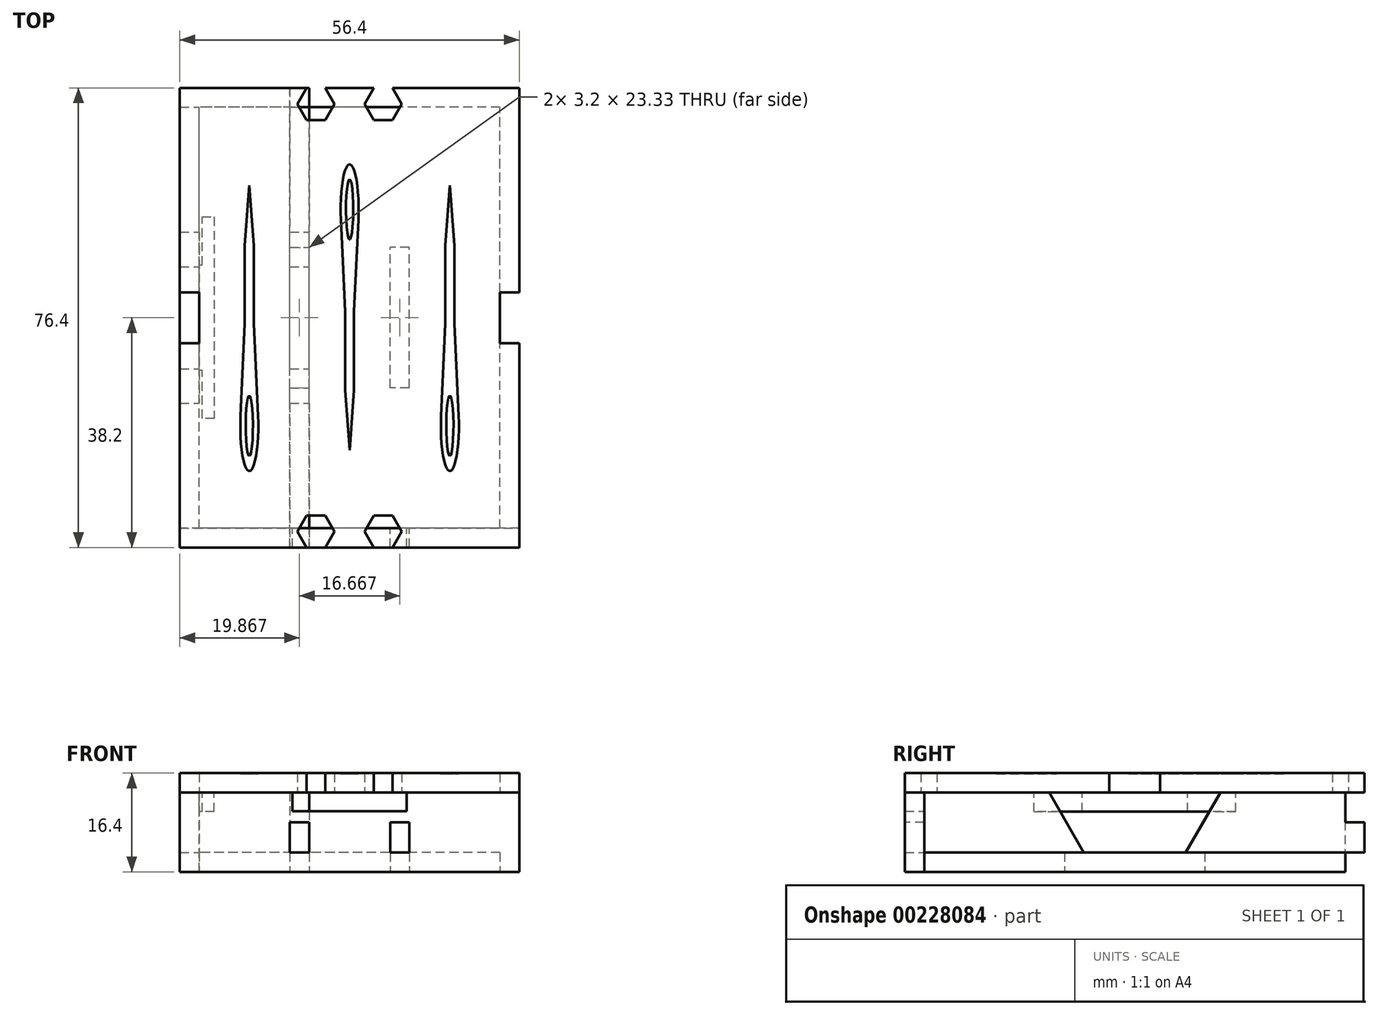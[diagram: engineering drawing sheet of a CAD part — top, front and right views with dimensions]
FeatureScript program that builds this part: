
annotation { "Feature Type Name" : "Feature", "Feature Type Description" : "" }
export const myFeature = defineFeature(function(context is Context, id is Id, definition is map)
    precondition{}
    {
        {
            assignVariable(context, id + "F0", {"name" : "mat_thickness", "anyValue" : 3.2 * mm});
        }
        {
            var Q0;
            Q0=qCreatedBy(makeId("Top.planeOp"),FACE);
            var sketch = newSketch(context, id + "F1", { "sketchPlane" : qUnion([Q0])});
            skLineSegment(sketch, "E0.bottom", {"start": v(25, -35) * mm, "end": v(-25, -35) * mm});
            skLineSegment(sketch, "E0.top", {"start": v(25, 35) * mm, "end": v(-25, 35) * mm});
            skLineSegment(sketch, "E0.left", {"start": v(25, -35) * mm, "end": v(25, 35) * mm});
            skLineSegment(sketch, "E0.right", {"start": v(-25, -35) * mm, "end": v(-25, 35) * mm});
            skPoint(sketch, "E0.middle", {"position": v(0, 0) * mm});
            skLineSegment(sketch, "E1.bottom", {"start": v(-6.73, -11.67) * mm, "end": v(-9.93, -11.67) * mm});
            skLineSegment(sketch, "E1.top", {"start": v(-6.73, 11.67) * mm, "end": v(-9.93, 11.67) * mm});
            skLineSegment(sketch, "E1.left", {"start": v(-6.73, -11.67) * mm, "end": v(-6.73, 11.67) * mm});
            skLineSegment(sketch, "E1.right", {"start": v(-9.93, -11.67) * mm, "end": v(-9.93, 11.67) * mm});
            skPoint(sketch, "E1.middle", {"position": v(-8.33, 0) * mm});
            skPoint(sketch, "E2.1.0.0", {"position": v(8.33, 0) * mm});
            skLineSegment(sketch, "E2.1.0.1", {"start": v(9.93, -11.67) * mm, "end": v(9.93, 11.67) * mm});
            skLineSegment(sketch, "E2.1.0.2", {"start": v(6.73, -11.67) * mm, "end": v(6.73, 11.67) * mm});
            skLineSegment(sketch, "E2.1.0.3", {"start": v(9.93, -11.67) * mm, "end": v(6.73, -11.67) * mm});
            skLineSegment(sketch, "E2.1.0.4", {"start": v(9.93, 11.67) * mm, "end": v(6.73, 11.67) * mm});
            skLineSegment(sketch, "E2.direction1", {"start": v(-9.93, -11.67) * mm, "end": v(6.73, -11.67) * mm, "construction": true});
            skSolve(sketch);
        }
        {
            var Q0;
            Q0=makeQuery(id+"F1.imprint","IMPRINT",FACE,{"disambiguationData":[TD([[makeQuery(id+"F1.imprint","IMPRINT",EDGE,{"derivedFrom":sQuery(id+"F1.wireOp",EDGE,"E0.bottom")}),-1.0]])]});
            extrude(context, id + "F2", {"entities" : qUnion([Q0]), "depth" : getVariable(context, 'mat_thickness')});
        }
        {
            var Q0;
            Q0=makeQuery(id+"F2.opExtrude","SWEPT_FACE",FACE,{"disambiguationData":[OSD([sQuery(id+"F1.wireOp",EDGE,"E0.right")])]});
            var sketch = newSketch(context, id + "F3", { "sketchPlane" : qUnion([Q0])});
            skLineSegment(sketch, "E3", {"start": v(-35, 0) * mm, "end": v(-35, 13.2) * mm});
            skLineSegment(sketch, "E4.0", {"start": v(35, 0) * mm, "end": v(-35, 0) * mm});
            skLineSegment(sketch, "E5", {"start": v(35, 0) * mm, "end": v(35, 13.2) * mm});
            skLineSegment(sketch, "E6", {"start": v(35, 13.2) * mm, "end": v(14.24, 13.2) * mm});
            skLineSegment(sketch, "E7", {"start": v(14.24, 13.2) * mm, "end": v(8.47, 3.2) * mm});
            skLineSegment(sketch, "E8", {"start": v(8.47, 3.2) * mm, "end": v(-8.47, 3.2) * mm});
            skLineSegment(sketch, "E9", {"start": v(-8.47, 3.2) * mm, "end": v(-14.24, 13.2) * mm});
            skLineSegment(sketch, "E10", {"start": v(-14.24, 13.2) * mm, "end": v(-35, 13.2) * mm});
            skLineSegment(sketch, "E11", {"start": v(0, -7.06) * mm, "end": v(0, 22.7) * mm, "construction": true});
            skSolve(sketch);
        }
        {
            var Q0;
            Q0 = qSketchRegion(id + "F3", true);
            extrude(context, id + "F4", {"entities" : qUnion([Q0]), "depth" : getVariable(context, 'mat_thickness')});
        }
        {
            var Q0;
            Q0=makeQuery(id+"F2.opExtrude","SWEPT_FACE",FACE,{"disambiguationData":[OSD([sQuery(id+"F1.wireOp",EDGE,"E1.left")])]});
            var sketch = newSketch(context, id + "F5", { "sketchPlane" : qUnion([Q0])});
            skLineSegment(sketch, "E12", {"start": v(38.2, 8.2) * mm, "end": v(38.2, 3.2) * mm});
            skLineSegment(sketch, "E13", {"start": v(38.2, 3.2) * mm, "end": v(35, 3.2) * mm});
            skLineSegment(sketch, "E14", {"start": v(35, 3.2) * mm, "end": v(35, 3.2) * mm});
            skLineSegment(sketch, "E15", {"start": v(35, 3.2) * mm, "end": v(11.67, 3.2) * mm});
            skLineSegment(sketch, "E16", {"start": v(11.67, 3.2) * mm, "end": v(11.67, 0) * mm});
            skLineSegment(sketch, "E17", {"start": v(11.67, 0) * mm, "end": v(-11.67, 0) * mm});
            skLineSegment(sketch, "E18", {"start": v(-11.67, 0) * mm, "end": v(-11.67, 3.2) * mm});
            skLineSegment(sketch, "E19", {"start": v(-11.67, 3.2) * mm, "end": v(-35, 3.2) * mm});
            skLineSegment(sketch, "E20", {"start": v(-35, 3.2) * mm, "end": v(-35, 3.2) * mm});
            skLineSegment(sketch, "E21", {"start": v(-35, 3.2) * mm, "end": v(-38.2, 3.2) * mm});
            skLineSegment(sketch, "E22", {"start": v(-38.2, 3.2) * mm, "end": v(-38.2, 8.2) * mm});
            skLineSegment(sketch, "E23", {"start": v(-38.2, 8.2) * mm, "end": v(-35, 8.2) * mm});
            skLineSegment(sketch, "E24", {"start": v(-35, 8.2) * mm, "end": v(-35, 13.2) * mm});
            skLineSegment(sketch, "E25", {"start": v(-35, 13.2) * mm, "end": v(35, 13.2) * mm});
            skLineSegment(sketch, "E26", {"start": v(35, 13.2) * mm, "end": v(35, 8.2) * mm});
            skLineSegment(sketch, "E27", {"start": v(35, 8.2) * mm, "end": v(38.2, 8.2) * mm});
            skLineSegment(sketch, "E28", {"start": v(0, -9.88) * mm, "end": v(0, 20.89) * mm, "construction": true});
            skPoint(sketch, "E28.startSnap0", {"position": v(0, 0) * mm});
            skLineSegment(sketch, "E29", {"start": v(14.24, 13.2) * mm, "end": v(8.47, 3.2) * mm});
            skLineSegment(sketch, "E30", {"start": v(8.47, 3.2) * mm, "end": v(-8.47, 3.2) * mm});
            skLineSegment(sketch, "E31", {"start": v(-8.47, 3.2) * mm, "end": v(-14.24, 13.2) * mm});
            skSolve(sketch);
        }
        {
            var Q0;
            Q0=makeQuery(id+"F5.imprint","IMPRINT",FACE,{"disambiguationData":[TD([[makeQuery(id+"F5.imprint","IMPRINT",EDGE,{"derivedFrom":sQuery(id+"F5.wireOp",EDGE,"E12")}),-1.0]])]});
            var Q1;
            {var subQ0=sQuery(id+"F5.wireOp",EDGE,"E19");Q1=makeQuery(id+"F5.imprint","IMPRINT",FACE,{"disambiguationData":[TD([[makeQuery(id+"F5.imprint","IMPRINT",EDGE,{"derivedFrom":subQ0}),-1.0]])]});}
            var Q2;
            {var subQ1=sQuery(id+"F5.wireOp",EDGE,"E16");Q2=makeQuery(id+"F5.imprint","IMPRINT",FACE,{"disambiguationData":[TD([[makeQuery(id+"F5.imprint","IMPRINT",EDGE,{"derivedFrom":subQ1}),-1.0]])]});}
            extrude(context, id + "F6", {"entities" : qUnion([Q0, Q1, Q2]), "depth" : getVariable(context, 'mat_thickness')});
        }
        {
            var Q0;
            Q0=makeQuery(id+"F2.opExtrude","SWEPT_FACE",FACE,{"disambiguationData":[OSD([sQuery(id+"F1.wireOp",EDGE,"E0.bottom")])]});
            var sketch = newSketch(context, id + "F7", { "sketchPlane" : qUnion([Q0])});
            skLineSegment(sketch, "E32.0", {"start": v(-28.2, 0) * mm, "end": v(-25, 0) * mm});
            skLineSegment(sketch, "E32.1", {"start": v(25, 0) * mm, "end": v(-25, 0) * mm});
            skLineSegment(sketch, "E32.2", {"start": v(-28.2, 0) * mm, "end": v(-28.2, 13.2) * mm});
            skLineSegment(sketch, "E33", {"start": v(-28.2, 13.2) * mm, "end": v(25, 13.2) * mm});
            skLineSegment(sketch, "E34", {"start": v(25, 13.2) * mm, "end": v(25, 0) * mm});
            skLineSegment(sketch, "E35.bottom", {"start": v(-6.73, 8.2) * mm, "end": v(-9.93, 8.2) * mm});
            skLineSegment(sketch, "E35.top", {"start": v(-6.73, 3.2) * mm, "end": v(-9.93, 3.2) * mm});
            skLineSegment(sketch, "E35.left", {"start": v(-6.73, 8.2) * mm, "end": v(-6.73, 3.2) * mm});
            skLineSegment(sketch, "E35.right", {"start": v(-9.93, 8.2) * mm, "end": v(-9.93, 3.2) * mm});
            skPoint(sketch, "E35.middle", {"position": v(-8.33, 5.7) * mm});
            skLineSegment(sketch, "E36", {"start": v(-25, 3.2) * mm, "end": v(-25, 13.2) * mm, "construction": true});
            skPoint(sketch, "E37.startSnap0", {"position": v(-25, 8.2) * mm});
            skLineSegment(sketch, "E38.1.0.0", {"start": v(9.93, 8.2) * mm, "end": v(9.93, 3.2) * mm});
            skLineSegment(sketch, "E38.1.0.1", {"start": v(6.73, 8.2) * mm, "end": v(6.73, 3.2) * mm});
            skLineSegment(sketch, "E38.1.0.2", {"start": v(9.93, 3.2) * mm, "end": v(6.73, 3.2) * mm});
            skPoint(sketch, "E38.1.0.3", {"position": v(8.33, 5.7) * mm});
            skLineSegment(sketch, "E38.1.0.4", {"start": v(9.93, 8.2) * mm, "end": v(6.73, 8.2) * mm});
            skLineSegment(sketch, "E38.direction1", {"start": v(-9.93, 3.2) * mm, "end": v(6.73, 3.2) * mm, "construction": true});
            skLineSegment(sketch, "E39", {"start": v(25, 13.2) * mm, "end": v(28.2, 13.2) * mm});
            skLineSegment(sketch, "E40", {"start": v(28.2, 13.2) * mm, "end": v(28.2, 0) * mm});
            skLineSegment(sketch, "E41", {"start": v(28.2, 0) * mm, "end": v(25, 0) * mm});
            skLineSegment(sketch, "E42", {"start": v(9.5, 13.2) * mm, "end": v(9.5, 10.1) * mm});
            skLineSegment(sketch, "E43", {"start": v(9.5, 10.1) * mm, "end": v(-9.5, 10.1) * mm});
            skLineSegment(sketch, "E44", {"start": v(-9.5, 10.1) * mm, "end": v(-9.5, 13.2) * mm});
            skLineSegment(sketch, "E45", {"start": v(0, -5.67) * mm, "end": v(0, 16.81) * mm, "construction": true});
            skSolve(sketch);
        }
        {
            var Q0;
            {var subQ0=sQuery(id+"F7.wireOp",EDGE,"E39");Q0=makeQuery(id+"F7.imprint","IMPRINT",FACE,{"disambiguationData":[TD([[makeQuery(id+"F7.imprint","IMPRINT",EDGE,{"derivedFrom":subQ0}),-1.0]])]});}
            var Q1;
            {var subQ2=sQuery(id+"F7.wireOp",EDGE,"E32.1");Q1=makeQuery(id+"F7.imprint","IMPRINT",FACE,{"disambiguationData":[TD([[makeQuery(id+"F7.imprint","IMPRINT",EDGE,{"derivedFrom":subQ2}),-1.0]])]});}
            var Q2;
            Q2=makeQuery(id+"F7.imprint","IMPRINT",FACE,{"disambiguationData":[TD([[makeQuery(id+"F7.imprint","IMPRINT",EDGE,{"derivedFrom":sQuery(id+"F7.wireOp",EDGE,"E32.0")}),1.0]])]});
            extrude(context, id + "F8", {"entities" : qUnion([Q0, Q1, Q2]), "depth" : getVariable(context, 'mat_thickness')});
        }
        {
            var Q0;
            Q0=makeQuery(id+"F4.opExtrude","CAP_FACE",FACE,{"disambiguationData":[OSD([sQuery(id+"F3.wireOp",EDGE,"E3"),sQuery(id+"F3.wireOp",EDGE,"E4.0"),sQuery(id+"F3.wireOp",EDGE,"E5"),sQuery(id+"F3.wireOp",EDGE,"E6"),sQuery(id+"F3.wireOp",EDGE,"E7"),sQuery(id+"F3.wireOp",EDGE,"E8"),sQuery(id+"F3.wireOp",EDGE,"E9"),sQuery(id+"F3.wireOp",EDGE,"E10")])],"isStart":false});
            var sketch = newSketch(context, id + "F9", { "sketchPlane" : qUnion([Q0])});
            skLineSegment(sketch, "E46.0", {"start": v(-8.47, 3.2) * mm, "end": v(-14.24, 13.2) * mm});
            skLineSegment(sketch, "E46.1", {"start": v(8.47, 3.2) * mm, "end": v(-8.47, 3.2) * mm});
            skLineSegment(sketch, "E46.2", {"start": v(14.24, 13.2) * mm, "end": v(8.47, 3.2) * mm});
            skLineSegment(sketch, "E47", {"start": v(-14.24, 13.2) * mm, "end": v(-4.23, 13.2) * mm});
            skLineSegment(sketch, "E48", {"start": v(-4.23, 13.2) * mm, "end": v(-4.23, 16.4) * mm});
            skLineSegment(sketch, "E49", {"start": v(-4.23, 16.4) * mm, "end": v(4.23, 16.4) * mm});
            skLineSegment(sketch, "E50", {"start": v(4.23, 16.4) * mm, "end": v(4.23, 13.2) * mm});
            skLineSegment(sketch, "E51", {"start": v(4.23, 13.2) * mm, "end": v(14.24, 13.2) * mm});
            skLineSegment(sketch, "E52", {"start": v(0, -3.65) * mm, "end": v(0, 23.25) * mm, "construction": true});
            skSolve(sketch);
        }
        {
            var Q0;
            Q0 = qSketchRegion(id + "F9", true);
            extrude(context, id + "F10", {"entities" : qUnion([Q0]), "oppositeDirection" : true, "depth" : getVariable(context, 'mat_thickness')});
        }
        {
            var Q0;
            Q0=makeQuery(id+"F8.opExtrude","SWEPT_FACE",FACE,{"disambiguationData":[OSD([sQuery(id+"F7.wireOp",EDGE,"E33"),sQuery(id+"F7.wireOp",EDGE,"E39")])]});
            var sketch = newSketch(context, id + "F11", { "sketchPlane" : qUnion([Q0])});
            skLineSegment(sketch, "E53.1", {"start": v(-28.2, 4.23) * mm, "end": v(-28.2, -4.23) * mm});
            skLineSegment(sketch, "E54", {"start": v(-28.2, -38.2) * mm, "end": v(-28.2, 38.2) * mm});
            skLineSegment(sketch, "E55", {"start": v(-28.2, 38.2) * mm, "end": v(28.2, 38.2) * mm});
            skLineSegment(sketch, "E56", {"start": v(28.2, 38.2) * mm, "end": v(28.2, -38.2) * mm});
            skLineSegment(sketch, "E57", {"start": v(-28.2, 4.23) * mm, "end": v(-25, 4.23) * mm});
            skLineSegment(sketch, "E58", {"start": v(-25, 4.23) * mm, "end": v(-25, -4.23) * mm});
            skLineSegment(sketch, "E59", {"start": v(-25, -4.23) * mm, "end": v(-28.2, -4.23) * mm});
            skLineSegment(sketch, "E60", {"start": v(28.2, 4.23) * mm, "end": v(25, 4.23) * mm});
            skLineSegment(sketch, "E61", {"start": v(25, 4.23) * mm, "end": v(25, -4.23) * mm});
            skPoint(sketch, "E61.endSnap0", {"position": v(-26.6, -4.23) * mm});
            skLineSegment(sketch, "E62", {"start": v(25, -4.23) * mm, "end": v(28.2, -4.23) * mm});
            skLineSegment(sketch, "E63", {"start": v(-28.2, -38.2) * mm, "end": v(28.2, -38.2) * mm});
            skPoint(sketch, "E64.0", {"position": v(-28.2, -38.2) * mm});
            skCircle(sketch, "E65.cCircle", {"center": v(5.59, -35.53) * mm, "radius": 3.09 * mm, "construction": true});
            skLineSegment(sketch, "E65.0", {"start": v(7.13, -38.2) * mm, "end": v(4.04, -38.2) * mm});
            skLineSegment(sketch, "E65.1", {"start": v(4.04, -38.2) * mm, "end": v(2.5, -35.53) * mm});
            skLineSegment(sketch, "E65.2", {"start": v(2.5, -35.53) * mm, "end": v(4.04, -32.85) * mm});
            skLineSegment(sketch, "E65.3", {"start": v(4.04, -32.85) * mm, "end": v(7.13, -32.85) * mm});
            skLineSegment(sketch, "E65.4", {"start": v(7.13, -32.85) * mm, "end": v(8.68, -35.53) * mm});
            skLineSegment(sketch, "E65.5", {"start": v(8.68, -35.53) * mm, "end": v(7.13, -38.2) * mm});
            skCircle(sketch, "E66.cCircle", {"center": v(-5.59, -35.53) * mm, "radius": 3.09 * mm, "construction": true});
            skLineSegment(sketch, "E66.0", {"start": v(-4.04, -38.2) * mm, "end": v(-7.13, -38.2) * mm});
            skLineSegment(sketch, "E66.1", {"start": v(-7.13, -38.2) * mm, "end": v(-8.68, -35.53) * mm});
            skLineSegment(sketch, "E66.2", {"start": v(-8.68, -35.53) * mm, "end": v(-7.13, -32.85) * mm});
            skLineSegment(sketch, "E66.3", {"start": v(-7.13, -32.85) * mm, "end": v(-4.04, -32.85) * mm});
            skLineSegment(sketch, "E66.4", {"start": v(-4.04, -32.85) * mm, "end": v(-2.5, -35.53) * mm});
            skLineSegment(sketch, "E66.5", {"start": v(-2.5, -35.53) * mm, "end": v(-4.04, -38.2) * mm});
            skCircle(sketch, "E67.cCircle", {"center": v(5.59, 35.52) * mm, "radius": 3.09 * mm, "construction": true});
            skLineSegment(sketch, "E67.0", {"start": v(7.13, 32.85) * mm, "end": v(4.04, 32.85) * mm});
            skLineSegment(sketch, "E67.1", {"start": v(4.04, 32.85) * mm, "end": v(2.5, 35.52) * mm});
            skLineSegment(sketch, "E67.2", {"start": v(2.5, 35.52) * mm, "end": v(4.04, 38.2) * mm});
            skLineSegment(sketch, "E67.3", {"start": v(4.04, 38.2) * mm, "end": v(7.13, 38.2) * mm});
            skLineSegment(sketch, "E67.4", {"start": v(7.13, 38.2) * mm, "end": v(8.68, 35.52) * mm});
            skLineSegment(sketch, "E67.5", {"start": v(8.68, 35.52) * mm, "end": v(7.13, 32.85) * mm});
            skCircle(sketch, "E68.cCircle", {"center": v(-5.59, 35.52) * mm, "radius": 3.09 * mm, "construction": true});
            skLineSegment(sketch, "E68.0", {"start": v(-4.04, 32.85) * mm, "end": v(-7.13, 32.85) * mm});
            skLineSegment(sketch, "E68.1", {"start": v(-7.13, 32.85) * mm, "end": v(-8.68, 35.52) * mm});
            skLineSegment(sketch, "E68.2", {"start": v(-8.68, 35.52) * mm, "end": v(-7.13, 38.2) * mm});
            skLineSegment(sketch, "E68.3", {"start": v(-7.13, 38.2) * mm, "end": v(-4.04, 38.2) * mm});
            skLineSegment(sketch, "E68.4", {"start": v(-4.04, 38.2) * mm, "end": v(-2.5, 35.52) * mm});
            skLineSegment(sketch, "E68.5", {"start": v(-2.5, 35.52) * mm, "end": v(-4.04, 32.85) * mm});
            skLineSegment(sketch, "E69", {"start": v(0, -50.78) * mm, "end": v(0, 51.28) * mm, "construction": true});
            skSolve(sketch);
        }
        {
            var Q0;
            {var subQ0=sQuery(id+"F11.wireOp",EDGE,"E53.0");Q0=makeQuery(id+"F11.imprint","IMPRINT",FACE,{"disambiguationData":[TD([[makeQuery(id+"F11.imprint","IMPRINT",EDGE,{"derivedFrom":subQ0}),1.0]])]});}
            var Q1;
            {var subQ7=sQuery(id+"F11.wireOp",EDGE,"E55");Q1=makeQuery(id+"F11.imprint","IMPRINT",FACE,{"disambiguationData":[TD([[makeQuery(id+"F11.imprint","IMPRINT",EDGE,{"derivedFrom":subQ7}),-1.0]])]});}
            var Q2;
            {var subQ1=sQuery(id+"F7.wireOp",EDGE,"E33");var subQ5=makeQuery(id+"F8.opExtrude","SWEPT_EDGE",EDGE,{"disambiguationData":[OSD([subQ1,sQuery(id+"F7.wireOp",EDGE,"E42")])]});Q2=makeQuery(id+"F11.imprint","IMPRINT",FACE,{"disambiguationData":[TD([[makeQuery(id+"F11.imprint","IMPRINT",EDGE,{"derivedFrom":subQ5}),-1.0]])]});}
            extrude(context, id + "F12", {"entities" : qUnion([Q0, Q1, Q2]), "depth" : getVariable(context, 'mat_thickness')});
        }
        {
            var Q0;
            Q0=makeQuery(id+"F12.opExtrude","CAP_FACE",FACE,{"disambiguationData":[OSD([sQuery(id+"F11.wireOp",EDGE,"E54"),sQuery(id+"F11.wireOp",EDGE,"E55"),sQuery(id+"F11.wireOp",EDGE,"E56"),sQuery(id+"F11.wireOp",EDGE,"E57"),sQuery(id+"F11.wireOp",EDGE,"E58"),sQuery(id+"F11.wireOp",EDGE,"E59"),sQuery(id+"F11.wireOp",EDGE,"E60"),sQuery(id+"F11.wireOp",EDGE,"E61"),sQuery(id+"F11.wireOp",EDGE,"E62"),sQuery(id+"F11.wireOp",EDGE,"E63"),sQuery(id+"F11.wireOp",EDGE,"E65.1"),sQuery(id+"F11.wireOp",EDGE,"E65.2"),sQuery(id+"F11.wireOp",EDGE,"E65.3"),sQuery(id+"F11.wireOp",EDGE,"E65.4"),sQuery(id+"F11.wireOp",EDGE,"E65.5"),sQuery(id+"F11.wireOp",EDGE,"E66.1"),sQuery(id+"F11.wireOp",EDGE,"E66.2"),sQuery(id+"F11.wireOp",EDGE,"E66.3"),sQuery(id+"F11.wireOp",EDGE,"E66.4"),sQuery(id+"F11.wireOp",EDGE,"E66.5"),sQuery(id+"F11.wireOp",EDGE,"E67.0"),sQuery(id+"F11.wireOp",EDGE,"E67.1"),sQuery(id+"F11.wireOp",EDGE,"E67.2"),sQuery(id+"F11.wireOp",EDGE,"E67.4"),sQuery(id+"F11.wireOp",EDGE,"E67.5"),sQuery(id+"F11.wireOp",EDGE,"E68.0"),sQuery(id+"F11.wireOp",EDGE,"E68.1"),sQuery(id+"F11.wireOp",EDGE,"E68.2"),sQuery(id+"F11.wireOp",EDGE,"E68.4"),sQuery(id+"F11.wireOp",EDGE,"E68.5")])],"isStart":false});
            var sketch = newSketch(context, id + "F13", { "sketchPlane" : qUnion([Q0])});
            skEllipse(sketch, "E70", {"center": v(-16.67, -18) * mm, "majorRadius": 5 * mm, "minorRadius": 0.6 * mm, "majorAxis": v(0, -1)});
            skEllipse(sketch, "E71", {"center": v(-16.67, -18) * mm, "majorRadius": 7.5 * mm, "minorRadius": 1.5 * mm, "majorAxis": v(0, -1)});
            skLineSegment(sketch, "E72", {"start": v(-15.2, -16.3) * mm, "end": v(-15.92, -1) * mm});
            skLineSegment(sketch, "E73", {"start": v(-15.92, -1) * mm, "end": v(-15.92, 12.03) * mm});
            skLineSegment(sketch, "E74", {"start": v(-15.92, 12.03) * mm, "end": v(-16.67, 22) * mm});
            skLineSegment(sketch, "E75", {"start": v(-16.67, 22) * mm, "end": v(-17.42, 12.03) * mm});
            skLineSegment(sketch, "E76", {"start": v(-17.42, 12.03) * mm, "end": v(-17.42, -1) * mm});
            skLineSegment(sketch, "E77", {"start": v(-17.42, -1) * mm, "end": v(-18.13, -16.3) * mm});
            skLineSegment(sketch, "E78.1.0.0", {"start": v(-0.75, 1) * mm, "end": v(-0.75, -12.03) * mm});
            skLineSegment(sketch, "E78.1.0.1", {"start": v(0.75, -12.03) * mm, "end": v(0.75, 1) * mm});
            skLineSegment(sketch, "E78.1.0.2", {"start": v(0.75, 1) * mm, "end": v(1.46, 16.3) * mm});
            skLineSegment(sketch, "E78.1.0.3", {"start": v(-1.46, 16.3) * mm, "end": v(-0.75, 1) * mm});
            skEllipse(sketch, "E78.1.0.4", {"center": v(0, 18) * mm, "majorRadius": 5 * mm, "minorRadius": 0.6 * mm, "majorAxis": v(0, 1)});
            skEllipse(sketch, "E78.1.0.5", {"center": v(0, 18) * mm, "majorRadius": 7.5 * mm, "minorRadius": 1.5 * mm, "majorAxis": v(0, 1)});
            skLineSegment(sketch, "E78.1.0.6", {"start": v(-0.75, -12.03) * mm, "end": v(0, -22) * mm});
            skLineSegment(sketch, "E78.1.0.7", {"start": v(0, -22) * mm, "end": v(0.75, -12.03) * mm});
            skLineSegment(sketch, "E78.2.0.0", {"start": v(17.42, -1) * mm, "end": v(17.42, 12.03) * mm});
            skLineSegment(sketch, "E78.2.0.1", {"start": v(15.92, 12.03) * mm, "end": v(15.92, -1) * mm});
            skLineSegment(sketch, "E78.2.0.2", {"start": v(15.92, -1) * mm, "end": v(15.2, -16.3) * mm});
            skLineSegment(sketch, "E78.2.0.3", {"start": v(18.13, -16.3) * mm, "end": v(17.42, -1) * mm});
            skEllipse(sketch, "E78.2.0.4", {"center": v(16.67, -18) * mm, "majorRadius": 5 * mm, "minorRadius": 0.6 * mm, "majorAxis": v(0, -1)});
            skEllipse(sketch, "E78.2.0.5", {"center": v(16.67, -18) * mm, "majorRadius": 7.5 * mm, "minorRadius": 1.5 * mm, "majorAxis": v(0, -1)});
            skLineSegment(sketch, "E78.2.0.6", {"start": v(17.42, 12.03) * mm, "end": v(16.67, 22) * mm});
            skLineSegment(sketch, "E78.2.0.7", {"start": v(16.67, 22) * mm, "end": v(15.92, 12.03) * mm});
            skLineSegment(sketch, "E78.direction1", {"start": v(-18.13, -16.3) * mm, "end": v(-1.46, -16.3) * mm, "construction": true});
            skSolve(sketch);
        }
        {
            var Q0;
            Q0 = qSketchRegion(id + "F13", true);
            extrude(context, id + "F14", {"entities" : qUnion([Q0]), "operationType" : NewBodyOperationType.REMOVE, "oppositeDirection" : true, "depth" : 0.1 * mm});
        }
        {
            var Q0;
            Q0=makeQuery(id+"F10.opExtrude","SWEPT_FACE",FACE,{"disambiguationData":[OSD([sQuery(id+"F9.wireOp",EDGE,"E47")])]});
            var sketch = newSketch(context, id + "F15", { "sketchPlane" : qUnion([Q0])});
            skLineSegment(sketch, "E79", {"start": v(-24.5, 16.75) * mm, "end": v(-22.5, 16.75) * mm});
            skLineSegment(sketch, "E80", {"start": v(-22.5, 16.75) * mm, "end": v(-22.5, -16.75) * mm});
            skLineSegment(sketch, "E81", {"start": v(-22.5, -16.75) * mm, "end": v(-24.5, -16.75) * mm});
            skLineSegment(sketch, "E82", {"start": v(-24.5, -16.75) * mm, "end": v(-24.5, -8.75) * mm});
            skLineSegment(sketch, "E83", {"start": v(-24.5, -8.75) * mm, "end": v(-25, -8.75) * mm});
            skLineSegment(sketch, "E84", {"start": v(-25, -8.75) * mm, "end": v(-25, 8.75) * mm});
            skLineSegment(sketch, "E85", {"start": v(-25, 8.75) * mm, "end": v(-24.5, 8.75) * mm});
            skLineSegment(sketch, "E86", {"start": v(-24.5, 8.75) * mm, "end": v(-24.5, 16.75) * mm});
            skPoint(sketch, "E87.0", {"position": v(-25, -14.24) * mm});
            skLineSegment(sketch, "E87.1", {"start": v(-28.2, 4.23) * mm, "end": v(-28.2, -4.23) * mm});
            skLineSegment(sketch, "E88", {"start": v(-34.36, 0) * mm, "end": v(-3.08, 0) * mm, "construction": true});
            skPoint(sketch, "E88.startSnap0", {"position": v(-28.2, 0) * mm});
            skSolve(sketch);
        }
        {
            var Q0;
            Q0 = qSketchRegion(id + "F15", true);
            extrude(context, id + "F16", {"entities" : qUnion([Q0]), "oppositeDirection" : true, "depth" : getVariable(context, 'mat_thickness')});
        }
    });
